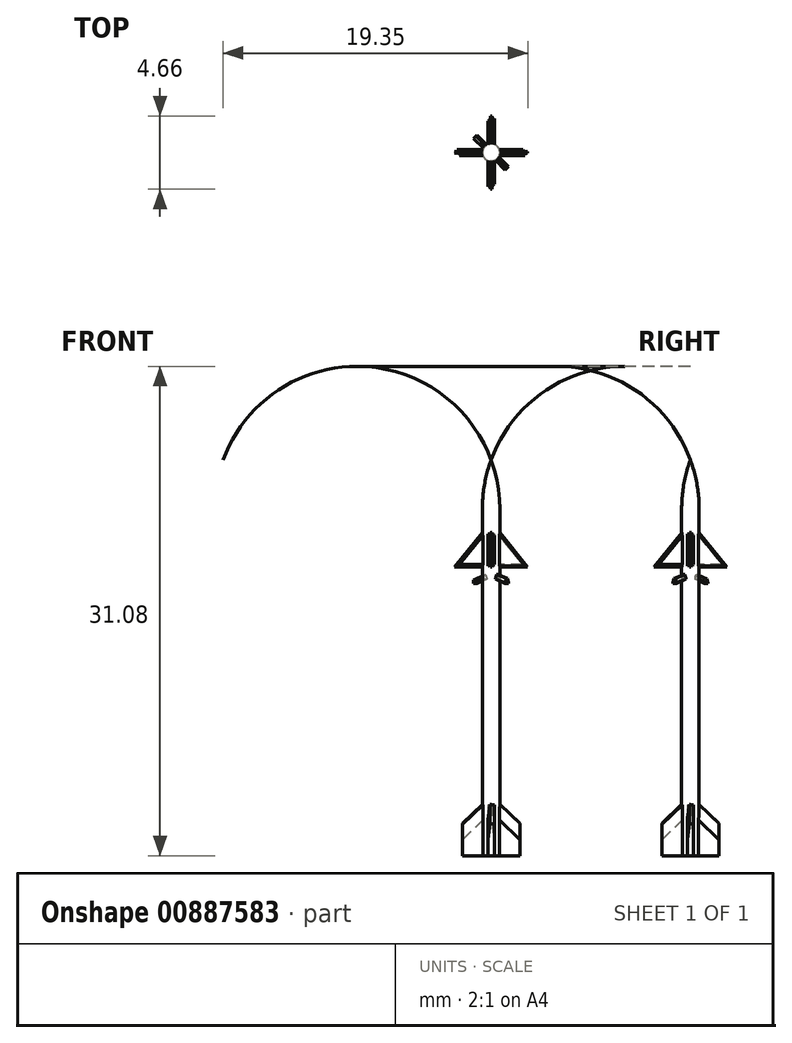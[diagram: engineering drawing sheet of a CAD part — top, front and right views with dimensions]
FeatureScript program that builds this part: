
annotation { "Feature Type Name" : "Feature", "Feature Type Description" : "" }
export const myFeature = defineFeature(function(context is Context, id is Id, definition is map)
    precondition{}
    {
        {
            var Q0;
            Q0=qCreatedBy(makeId("Front.planeOp"),FACE);
            var sketch = newSketch(context, id + "F0", { "sketchPlane" : qUnion([Q0])});
            skLineSegment(sketch, "E0", {"start": v(0, 0) * mm, "end": v(0, 25.14) * mm});
            skLineSegment(sketch, "E1", {"start": v(0.56, 22.01) * mm, "end": v(0.56, 0) * mm});
            skLineSegment(sketch, "E2", {"start": v(0.56, 0) * mm, "end": v(0, 0) * mm});
            skArc(sketch, "E3", {"start": v(0.56, 22.01) * mm, "mid": v(0.42, 23.6) * mm, "end": v(0, 25.14) * mm});
            skSolve(sketch);
        }
        {
            var Q0;
            Q0=qSketchRegion(id+"F0",true);
            var Q1;
            Q1=sQuery(id+"F0.wireOp",EDGE,"E0");
            revolve(context, id + "F1", {"surfaceOperationType" : NewSurfaceOperationType.NEW, "entities" : qUnion([Q0]), "axis" : qUnion([Q1]), "revolveType" : RevolveType.FULL});
        }
        {
            var Q0;
            Q0=qCreatedBy(makeId("Front.planeOp"),FACE);
            var sketch = newSketch(context, id + "F2", { "sketchPlane" : qUnion([Q0])});
            skLineSegment(sketch, "E4", {"start": v(-0.56, 0.9) * mm, "end": v(-0.56, 22.01) * mm, "construction": true});
            skLineSegment(sketch, "E5.0", {"start": v(0.56, 22.01) * mm, "end": v(-0.56, 22.01) * mm});
            skLineSegment(sketch, "E6", {"start": v(-0.25, 20.9) * mm, "end": v(-2.33, 18.33) * mm});
            skLineSegment(sketch, "E7", {"start": v(-2.33, 18.33) * mm, "end": v(2.33, 18.33) * mm});
            skLineSegment(sketch, "E8", {"start": v(2.33, 18.33) * mm, "end": v(0.25, 20.9) * mm});
            skLineSegment(sketch, "E9", {"start": v(0.25, 20.9) * mm, "end": v(-0.25, 20.9) * mm});
            skLineSegment(sketch, "E10.0", {"start": v(0.56, 0) * mm, "end": v(-0.56, 0) * mm});
            skLineSegment(sketch, "E11", {"start": v(-1.82, 0) * mm, "end": v(-1.82, 2.19) * mm});
            skLineSegment(sketch, "E12", {"start": v(-1.82, 2.19) * mm, "end": v(-0.25, 3.7) * mm});
            skLineSegment(sketch, "E13", {"start": v(-0.25, 3.7) * mm, "end": v(0.25, 3.7) * mm});
            skLineSegment(sketch, "E14", {"start": v(1.82, 2.19) * mm, "end": v(1.82, 0) * mm});
            skLineSegment(sketch, "E15", {"start": v(0, 0) * mm, "end": v(0, 0) * mm});
            skLineSegment(sketch, "E16", {"start": v(0, 0) * mm, "end": v(0, 3.7) * mm, "construction": true});
            skPoint(sketch, "E16.endSnap0", {"position": v(0, 0) * mm});
            skLineSegment(sketch, "E17", {"start": v(0, 22.01) * mm, "end": v(0, 20.9) * mm, "construction": true});
            skLineSegment(sketch, "E18", {"start": v(0, 22.01) * mm, "end": v(0, 18.33) * mm, "construction": true});
            skPoint(sketch, "E19", {"position": v(-0.56, 20.52) * mm});
            skPoint(sketch, "E20", {"position": v(-0.56, 3.4) * mm});
            skLineSegment(sketch, "E21", {"start": v(1.82, 2.19) * mm, "end": v(0.25, 3.7) * mm});
            skLineSegment(sketch, "E22", {"start": v(-1.82, 0) * mm, "end": v(1.82, 0) * mm});
            skSolve(sketch);
        }
        {
            var Q0;
            Q0=qSketchRegion(id+"F2",true);
            extrude(context, id + "F3", {"entities" : qUnion([Q0]), "operationType" : NewBodyOperationType.ADD, "depth" : .4 * mm, "offsetDistance" : 25 * mm, "symmetric" : true});
        }
        {
            var Q0;
            Q0=makeQuery(id+"F3.opExtrude","CAP_EDGE",EDGE,{"disambiguationData":[OSD([sQuery(id+"F2.wireOp",EDGE,"E8")])],"isStart":false});
            var Q1;
            Q1=makeQuery(id+"F3.opExtrude","CAP_EDGE",EDGE,{"disambiguationData":[OSD([sQuery(id+"F2.wireOp",EDGE,"E8")])],"isStart":true});
            var Q2;
            Q2=makeQuery(id+"F3.opExtrude","CAP_EDGE",EDGE,{"disambiguationData":[OSD([sQuery(id+"F2.wireOp",EDGE,"E6")])],"isStart":false});
            var Q3;
            {var subQ0=sQuery(id+"F2.wireOp",EDGE,"E7");var subQ1=sQuery(id+"F2.wireOp",EDGE,"E6");Q3=makeQuery(id+"F3.boolean.opBoolean","SPLIT",EDGE,{"disambiguationData":[TD([makeQuery(id+"F3.opExtrude","SWEPT_FACE",FACE,{"disambiguationData":[OSD([subQ1])]})])],"derivedFrom":makeQuery(id+"F3.opExtrude","CAP_EDGE",EDGE,{"disambiguationData":[OSD([subQ0])],"isStart":false})});}
            var Q4;
            Q4=makeQuery(id+"F3.opExtrude","CAP_EDGE",EDGE,{"disambiguationData":[OSD([sQuery(id+"F2.wireOp",EDGE,"E21")])],"isStart":false});
            var Q5;
            Q5=makeQuery(id+"F3.opExtrude","CAP_EDGE",EDGE,{"disambiguationData":[OSD([sQuery(id+"F2.wireOp",EDGE,"E12")])],"isStart":true});
            chamfer(context, id + "F4", {"entities" : qUnion([Q0, Q1, Q2, Q3, Q4, Q5]), "chamferType" : ChamferType.OFFSET_ANGLE, "width" : .15 * mm, "oppositeDirection" : true, "angle" : 80 * degree, "tangentPropagation" : true});
        }
        {
            var Q0;
            {var subQ0=sQuery(id+"F2.wireOp",EDGE,"E8");var subQ1=sQuery(id+"F2.wireOp",EDGE,"E7");Q0=makeQuery(id+"F3.boolean.opBoolean","SPLIT",EDGE,{"disambiguationData":[TD([makeQuery(id+"F3.opExtrude","SWEPT_FACE",FACE,{"disambiguationData":[OSD([subQ0])]})])],"derivedFrom":makeQuery(id+"F3.opExtrude","CAP_EDGE",EDGE,{"disambiguationData":[OSD([subQ1])],"isStart":false})});}
            var Q1;
            {var subQ0=sQuery(id+"F2.wireOp",EDGE,"E8");var subQ1=sQuery(id+"F2.wireOp",EDGE,"E7");Q1=makeQuery(id+"F3.boolean.opBoolean","SPLIT",EDGE,{"disambiguationData":[TD([makeQuery(id+"F3.opExtrude","SWEPT_FACE",FACE,{"disambiguationData":[OSD([subQ0])]})])],"derivedFrom":makeQuery(id+"F3.opExtrude","CAP_EDGE",EDGE,{"disambiguationData":[OSD([subQ1])],"isStart":true})});}
            chamfer(context, id + "F5", {"entities" : qUnion([Q0, Q1]), "chamferType" : ChamferType.OFFSET_ANGLE, "width" : .15 * mm, "oppositeDirection" : true, "angle" : 80 * degree, "tangentPropagation" : true});
        }
        {
            var Q0;
            Q0=makeQuery(id+"F3.opExtrude","CAP_EDGE",EDGE,{"disambiguationData":[OSD([sQuery(id+"F2.wireOp",EDGE,"E21")])],"isStart":true});
            var Q1;
            Q1=makeQuery(id+"F3.opExtrude","CAP_EDGE",EDGE,{"disambiguationData":[OSD([sQuery(id+"F2.wireOp",EDGE,"E12")])],"isStart":false});
            var Q2;
            Q2=makeQuery(id+"F3.opExtrude","CAP_EDGE",EDGE,{"disambiguationData":[OSD([sQuery(id+"F2.wireOp",EDGE,"E6")])],"isStart":true});
            var Q3;
            {var subQ0=sQuery(id+"F2.wireOp",EDGE,"E6");var subQ1=sQuery(id+"F2.wireOp",EDGE,"E7");Q3=makeQuery(id+"F3.boolean.opBoolean","SPLIT",EDGE,{"disambiguationData":[TD([makeQuery(id+"F3.opExtrude","SWEPT_FACE",FACE,{"disambiguationData":[OSD([subQ0])]})])],"derivedFrom":makeQuery(id+"F3.opExtrude","CAP_EDGE",EDGE,{"disambiguationData":[OSD([subQ1])],"isStart":true})});}
            chamfer(context, id + "F6", {"entities" : qUnion([Q0, Q1, Q2, Q3]), "chamferType" : ChamferType.OFFSET_ANGLE, "width" : .15 * mm, "oppositeDirection" : false, "angle" : 80 * degree, "tangentPropagation" : true});
        }
        {
            var Q0;
            Q0=makeQuery(id+"F1.opRevolve","SWEPT_BODY",BODY,{"disambiguationData":[OSD([sQuery(id+"F0.wireOp",EDGE,"E0"),sQuery(id+"F0.wireOp",EDGE,"E1"),sQuery(id+"F0.wireOp",EDGE,"E2"),sQuery(id+"F0.wireOp",EDGE,"m1K1lCZm-MTc8-Btmt-IA6e-LtdyprMEJuD3")])]});
            var Q1;
            Q1=makeQuery(id+"F1.opRevolve","SWEPT_FACE",FACE,{"disambiguationData":[OSD([sQuery(id+"F0.wireOp",EDGE,"E1")])]});
            circularPattern(context, id + "F7", {"entities" : qUnion([Q0]), "axis" : qUnion([Q1]), "angle" : 360 * degree, "instanceCount" : 4, "equalSpace" : true, "computeTransformsWithoutBuiltin" : true});
        }
        {
            var Q0;
            Q0=qCreatedBy(makeId("Front.planeOp"),FACE);
            var Q1;
            Q1=qCreatedBy(makeId("Right.planeOp"),FACE);
            cPlane(context, id + "F8", {"entities" : qUnion([Q0, Q1]), "cplaneType" : CPlaneType.MID_PLANE, "offset" : 25 * mm, "width" : 150 * mm, "height" : 150 * mm});
        }
        {
            var Q0;
            Q0=qCreatedBy(id+"F8.planeOp",FACE);
            var sketch = newSketch(context, id + "F9", { "sketchPlane" : qUnion([Q0])});
            skLineSegment(sketch, "E23", {"start": v(-0.25, 17.96) * mm, "end": v(-1.41, 17.6) * mm});
            skLineSegment(sketch, "E24", {"start": v(1.41, 17.6) * mm, "end": v(0.25, 17.96) * mm});
            skLineSegment(sketch, "E25", {"start": v(0.25, 17.96) * mm, "end": v(-0.25, 17.96) * mm});
            skPoint(sketch, "E26", {"position": v(-0.5, 17.88) * mm});
            skLineSegment(sketch, "E27", {"start": v(0, 0) * mm, "end": v(0, 17.65) * mm, "construction": true});
            skPoint(sketch, "E27.endSnap0", {"position": v(0, 17.65) * mm});
            skLineSegment(sketch, "E28", {"start": v(-1.41, 17.6) * mm, "end": v(-1.41, 17.3) * mm});
            skLineSegment(sketch, "E29", {"start": v(-1.41, 17.3) * mm, "end": v(-0.25, 17.65) * mm});
            skLineSegment(sketch, "E30", {"start": v(-0.25, 17.65) * mm, "end": v(0.25, 17.65) * mm});
            skLineSegment(sketch, "E31", {"start": v(0.25, 17.65) * mm, "end": v(1.41, 17.3) * mm});
            skLineSegment(sketch, "E32", {"start": v(1.41, 17.3) * mm, "end": v(1.41, 17.6) * mm});
            skPoint(sketch, "E33", {"position": v(0, 17.96) * mm});
            skLineSegment(sketch, "E34.0.0", {"start": v(0.56, 0) * mm, "end": v(0.56, 0) * mm});
            skLineSegment(sketch, "E34.0.1", {"start": v(0.5, 0) * mm, "end": v(0.53, 0) * mm});
            skLineSegment(sketch, "E34.0.2", {"start": v(0.53, 0) * mm, "end": v(0.25, 0) * mm});
            skLineSegment(sketch, "E34.0.3", {"start": v(0.25, 0) * mm, "end": v(0.23, 0) * mm});
            skLineSegment(sketch, "E34.0.4", {"start": v(0.23, 0) * mm, "end": v(-0.56, 0) * mm});
            skLineSegment(sketch, "E34.0.5", {"start": v(0.25, 0) * mm, "end": v(-0.5, 0) * mm});
            skLineSegment(sketch, "E34.0.6", {"start": v(0.25, 0) * mm, "end": v(0.53, 0) * mm});
            skLineSegment(sketch, "E34.0.7", {"start": v(0.53, 0) * mm, "end": v(0.56, 0) * mm});
            skSolve(sketch);
        }
        {
            var Q0;
            Q0=qSketchRegion(id+"F9",true);
            extrude(context, id + "F10", {"entities" : qUnion([Q0]), "operationType" : NewBodyOperationType.ADD, "depth" : .3 * mm, "offsetDistance" : 25 * mm, "symmetric" : true});
        }
        {
            var Q0;
            Q0=makeQuery(id+"F10.opExtrude","CAP_EDGE",EDGE,{"disambiguationData":[OSD([sQuery(id+"F9.wireOp",EDGE,"E24")])],"isStart":false});
            var Q1;
            Q1=makeQuery(id+"F10.opExtrude","CAP_EDGE",EDGE,{"disambiguationData":[OSD([sQuery(id+"F9.wireOp",EDGE,"E24")])],"isStart":true});
            var Q2;
            Q2=makeQuery(id+"F10.opExtrude","CAP_EDGE",EDGE,{"disambiguationData":[OSD([sQuery(id+"F9.wireOp",EDGE,"E23")])],"isStart":false});
            chamfer(context, id + "F11", {"entities" : qUnion([Q0, Q1, Q2]), "chamferType" : ChamferType.OFFSET_ANGLE, "width" : .1 * mm, "oppositeDirection" : true, "angle" : 70 * degree, "tangentPropagation" : true});
        }
        {
            var Q0;
            Q0=makeQuery(id+"F10.opExtrude","CAP_EDGE",EDGE,{"disambiguationData":[OSD([sQuery(id+"F9.wireOp",EDGE,"E23")])],"isStart":true});
            chamfer(context, id + "F12", {"entities" : qUnion([Q0]), "chamferType" : ChamferType.OFFSET_ANGLE, "width" : .1 * mm, "oppositeDirection" : false, "angle" : 70 * degree, "tangentPropagation" : true});
        }
    });
